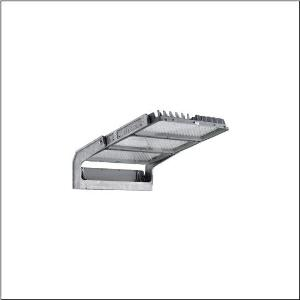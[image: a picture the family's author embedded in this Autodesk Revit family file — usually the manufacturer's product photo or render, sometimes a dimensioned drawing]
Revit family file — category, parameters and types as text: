
# Revit family: floodlight_fl_11_maxi_pro___rs08_5xa779129l02fb_e772
name_source: partatom
category: Lighting Fixtures
units: mm (PartAtom-declared; Revit-internal decimal feet)

## family parameters
Cut with Voids When Loaded = No
Host = Face
Light Source = No
Part Type = Normal
Room Calculation Point = No
Round Connector Dimension = Use Diameter
Shared = No

## types (1)
- --- (1 x LED, 171610 lm, 1400 W, 5700K)
    Apparent Load = 1400 VA
    CIE Flux Codes = 70 87 98 100 100
    Color Rendering = 70
    Color Temperature = 5700K
    Default Elevation = 1800 mm
    Description = Floodlight FL 11  maxi  pro floodlight; light control with lens of PMMA; cover panel of toughened safety glass, transparent; light distribution: RS08, rotationally symmetric direct distribution, LED; colour temperature: 5700K, rated luminous flux: 171.610lm, colour rendering: CRI > 70, light colour: 757; luminous efficacy: 123lm/W; brightness control: DALI 2; with terminal, 5-pole, max. 2.5mm², mains connection: 220..240V/380..400V AC, 50/60Hz, surge voltage resistance: line to ground: 10kV, LED service life up to 100,000h L90. Typical operating time: 1000h per year., ECG replaceable separately, LED unit replaceable without ESD environment, dustproof LED module, dimming range 10..100%; 1400W floodlight with 3x LED unit of diecast aluminium, coated grey; length: 1.003mm / width: 651mm / height: 338mm; mounting bracket, of diecast aluminium, uncoated, natural, equipment: Power, protection rating (complete): IP66; insulation class (complete): insulation class I (protective earthing); certification: CE, ENEC, VDE; ball protection: ball impact resistant, only for outdoor installations in the designated locations, permissible operating ambient temperature: -45..+55°C, permissible storage temperature: -40..+85°Cpackaging unit: 1 piece

Light Distribution: RS08
    Height = 320 mm
    Lamp = 1 x LED
    Lamp Light Flux = 171610 lm
    Lamp Power = 1400 W
    Lamp count = 1
    Length = 1002 mm
    Luminous efficacy = 123 lm/W
    Manufacturer = Siteco
    ModVariant = No
    Model = 5XA779129L02FB
    Mounting Place = Ceiling
    Mounting Type = Surface mounted
    Number of Poles = 1
    OnlyDefault = Yes
    Power Factor = 1
    Product Name = Floodlight FL 11 maxi pro | RS08
    Product group = floodlight | ceiling mounted
    ProductGroupID = 303
    Protection Class = Protection class I
    Protection Degree = IP 66
    RLX_Detail_Level = 1
    RLX_Emergency_Light_Flux = 0 lm
    RLX_Emergency_Type = 0
    RLX_Emergency_Type_DB = No
    RlxData = <blob elided: 40441 chars, md5=1e9fef77>
    Socket = socket
    Standby Power = 0 W
    System Light Flux = 171610 lm
    System Power = 1400 W
    Type Comments = factory setting: luminous flux: 100 % | dim-lin: 254 | 955 mA
    Type Image = l_1356210.jpg
    URL = http://relux.com
    VarID = @adj_040103
    Voltage = 0 V
    Weight = 0.00 kg
    Width = 655 mm

## geometry (parser evidence)
native form markers: Blend x4, Sweep x12
no freeform markers — native parametric forms only
